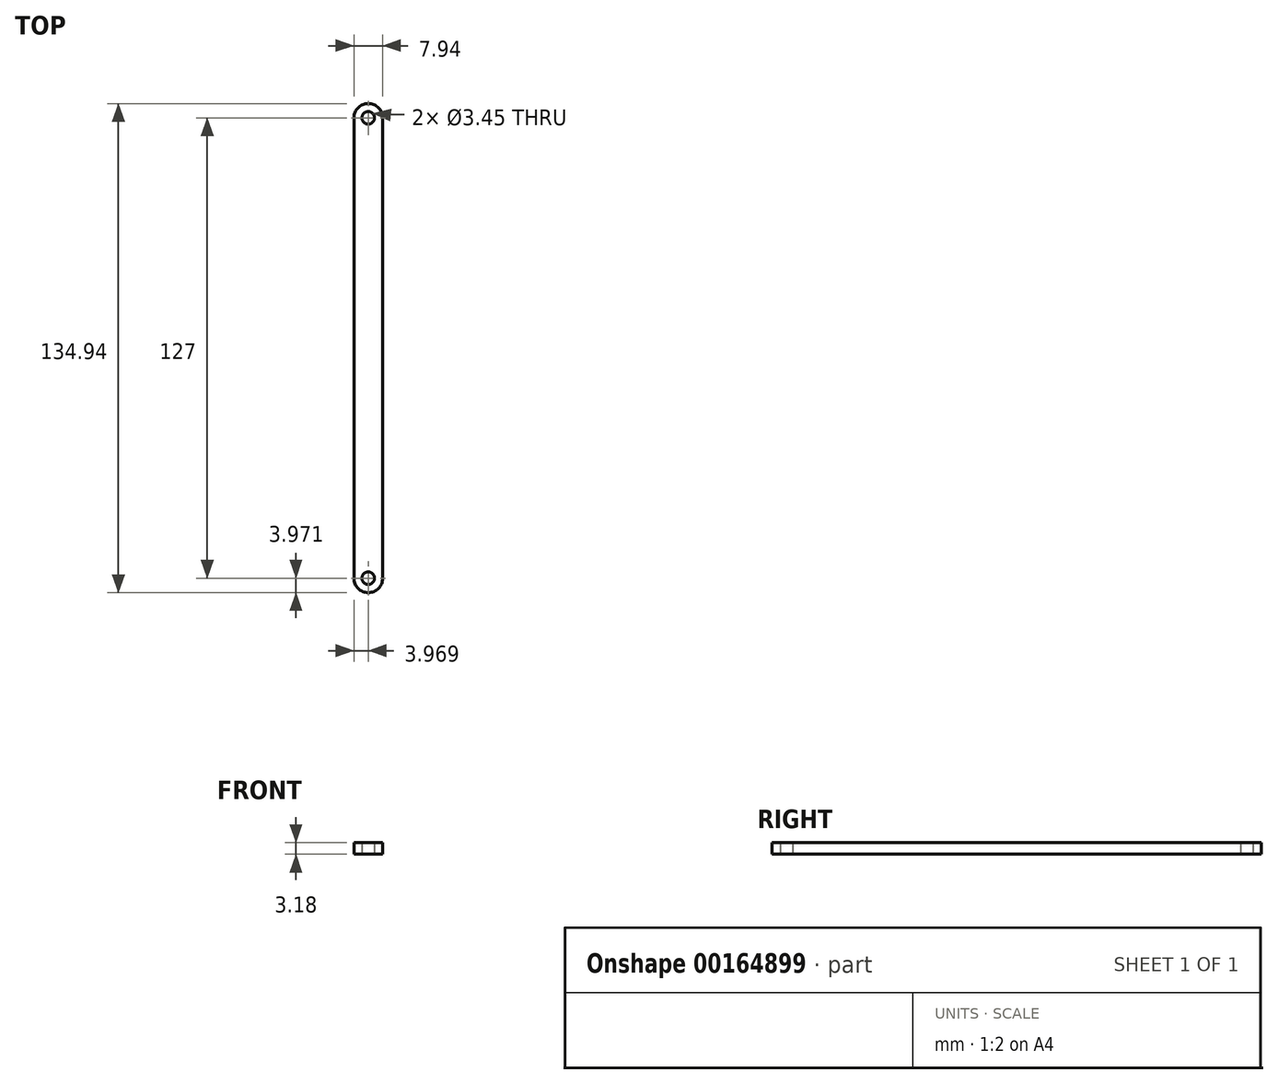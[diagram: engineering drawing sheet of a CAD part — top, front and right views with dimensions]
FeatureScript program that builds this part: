
annotation { "Feature Type Name" : "Feature", "Feature Type Description" : "" }
export const myFeature = defineFeature(function(context is Context, id is Id, definition is map)
    precondition{}
    {
        {
            var Q0;
            Q0=qCreatedBy(makeId("Top.planeOp"),FACE);
            var sketch = newSketch(context, id + "F0", { "sketchPlane" : qUnion([Q0])});
            skLineSegment(sketch, "E0.bottom", {"start": v(0, 0) * mm, "end": v(7.94, 0) * mm});
            skLineSegment(sketch, "E0.top", {"start": v(0, -134.94) * mm, "end": v(7.94, -134.94) * mm});
            skLineSegment(sketch, "E0.left", {"start": v(0, 0) * mm, "end": v(0, -134.94) * mm});
            skLineSegment(sketch, "E0.right", {"start": v(7.94, 0) * mm, "end": v(7.94, -134.94) * mm});
            skLineSegment(sketch, "E1", {"start": v(3.97, 0) * mm, "end": v(3.97, -3.97) * mm, "construction": true});
            skLineSegment(sketch, "E2", {"start": v(3.97, -3.97) * mm, "end": v(7.94, -3.97) * mm, "construction": true});
            skLineSegment(sketch, "E3", {"start": v(3.97, -134.94) * mm, "end": v(3.97, -130.97) * mm, "construction": true});
            skCircle(sketch, "E4", {"center": v(3.97, -3.97) * mm, "radius": 1.73 * mm});
            skCircle(sketch, "E5", {"center": v(3.97, -130.97) * mm, "radius": 1.73 * mm});
            skSolve(sketch);
        }
        {
            var Q0;
            Q0=qSketchRegion(id+"F0",true);
            extrude(context, id + "F1", {"entities" : qUnion([Q0]), "depth" : 3.17 * mm});
        }
        {
            var Q0;
            Q0=makeQuery(id+"F1.opExtrude","SWEPT_EDGE",EDGE,{"disambiguationData":[OSD([sQuery(id+"F0.wireOp",EDGE,"E0.bottom"),sQuery(id+"F0.wireOp",EDGE,"E0.right")])]});
            var Q1;
            Q1=makeQuery(id+"F1.opExtrude","SWEPT_EDGE",EDGE,{"disambiguationData":[OSD([sQuery(id+"F0.wireOp",EDGE,"E0.bottom"),sQuery(id+"F0.wireOp",EDGE,"E0.left")])]});
            var Q2;
            Q2=makeQuery(id+"F1.opExtrude","SWEPT_EDGE",EDGE,{"disambiguationData":[OSD([sQuery(id+"F0.wireOp",EDGE,"E0.top"),sQuery(id+"F0.wireOp",EDGE,"E0.left")])]});
            var Q3;
            Q3=makeQuery(id+"F1.opExtrude","SWEPT_EDGE",EDGE,{"disambiguationData":[OSD([sQuery(id+"F0.wireOp",EDGE,"E0.top"),sQuery(id+"F0.wireOp",EDGE,"E0.right")])]});
            fillet(context, id + "F2", {"entities" : qUnion([Q0, Q1, Q2, Q3]), "radius" : 3.97 * mm, "tangentPropagation" : true, "allowEdgeOverflow" : false});
        }
    });
